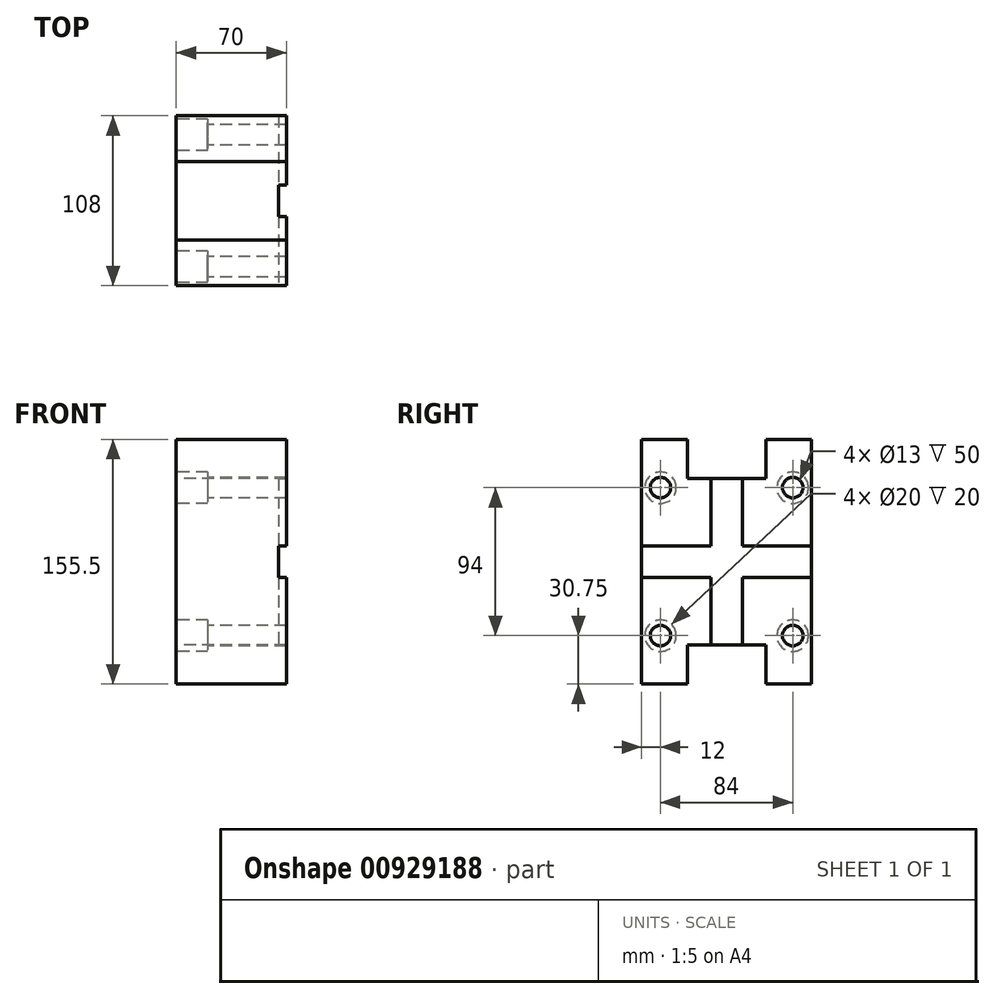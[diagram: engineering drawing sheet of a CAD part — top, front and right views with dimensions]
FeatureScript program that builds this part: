
annotation { "Feature Type Name" : "Feature", "Feature Type Description" : "" }
export const myFeature = defineFeature(function(context is Context, id is Id, definition is map)
    precondition{}
    {
        {
            var Q0;
            Q0=qCreatedBy(makeId("Right.planeOp"),FACE);
            var sketch = newSketch(context, id + "F0", { "sketchPlane" : qUnion([Q0])});
            skLineSegment(sketch, "E0.bottom", {"start": v(54, 77.75) * mm, "end": v(-54, 77.75) * mm});
            skLineSegment(sketch, "E0.top", {"start": v(54, -77.75) * mm, "end": v(-54, -77.75) * mm});
            skLineSegment(sketch, "E0.left", {"start": v(54, 77.75) * mm, "end": v(54, -77.75) * mm});
            skLineSegment(sketch, "E0.right", {"start": v(-54, 77.75) * mm, "end": v(-54, -77.75) * mm});
            skPoint(sketch, "E0.middle", {"position": v(0, 0) * mm});
            skSolve(sketch);
        }
        {
            var Q0;
            Q0 = qSketchRegion(id + "F0", true);
            extrude(context, id + "F1", {"entities" : qUnion([Q0]), "oppositeDirection" : true, "depth" : 70 * mm, "offsetDistance" : 25 * mm});
        }
        {
            var Q0;
            Q0=makeQuery(id+"F1.opExtrude","CAP_FACE",FACE,{"disambiguationData":[OSD([sQuery(id+"F0.wireOp",EDGE,"E0.bottom"),sQuery(id+"F0.wireOp",EDGE,"E0.top"),sQuery(id+"F0.wireOp",EDGE,"E0.left"),sQuery(id+"F0.wireOp",EDGE,"E0.right")])],"isStart":false});
            var sketch = newSketch(context, id + "F2", { "sketchPlane" : qUnion([Q0])});
            skCircle(sketch, "E1", {"center": v(-42, 47) * mm, "radius": 6.5 * mm});
            skCircle(sketch, "E2.MirrorC", {"center": v(42, 47) * mm, "radius": 6.5 * mm});
            skCircle(sketch, "E3.MirrorC", {"center": v(-42, -47) * mm, "radius": 6.5 * mm});
            skCircle(sketch, "E4.MirrorC", {"center": v(42, -47) * mm, "radius": 6.5 * mm});
            skSolve(sketch);
        }
        {
            var Q0;
            Q0 = qSketchRegion(id + "F2", true);
            extrude(context, id + "F3", {"entities" : qUnion([Q0]), "operationType" : NewBodyOperationType.REMOVE, "endBound" : BoundingType.THROUGH_ALL, "oppositeDirection" : true, "depth" : 25 * mm, "offsetDistance" : 25 * mm});
        }
        {
            var Q0;
            Q0=makeQuery(id+"F1.opExtrude","CAP_FACE",FACE,{"disambiguationData":[OSD([sQuery(id+"F0.wireOp",EDGE,"E0.bottom"),sQuery(id+"F0.wireOp",EDGE,"E0.top"),sQuery(id+"F0.wireOp",EDGE,"E0.left"),sQuery(id+"F0.wireOp",EDGE,"E0.right")])],"isStart":false});
            var sketch = newSketch(context, id + "F4", { "sketchPlane" : qUnion([Q0])});
            skLineSegment(sketch, "E5.bottom", {"start": v(25, 77.75) * mm, "end": v(-25, 77.75) * mm});
            skLineSegment(sketch, "E5.top", {"start": v(25, 52.75) * mm, "end": v(-25, 52.75) * mm});
            skLineSegment(sketch, "E5.left", {"start": v(25, 77.75) * mm, "end": v(25, 52.75) * mm});
            skLineSegment(sketch, "E5.right", {"start": v(-25, 77.75) * mm, "end": v(-25, 52.75) * mm});
            skPoint(sketch, "E5.middle", {"position": v(0, 65.25) * mm});
            skLineSegment(sketch, "E6.MirrorCS", {"start": v(25, -52.75) * mm, "end": v(-25, -52.75) * mm});
            skLineSegment(sketch, "E7.MirrorCS", {"start": v(-25, -77.75) * mm, "end": v(-25, -52.75) * mm});
            skLineSegment(sketch, "E8.MirrorCS", {"start": v(25, -77.75) * mm, "end": v(-25, -77.75) * mm});
            skLineSegment(sketch, "E9.MirrorCS", {"start": v(25, -77.75) * mm, "end": v(25, -52.75) * mm});
            skSolve(sketch);
        }
        {
            var Q0;
            Q0 = qSketchRegion(id + "F4", true);
            extrude(context, id + "F5", {"entities" : qUnion([Q0]), "operationType" : NewBodyOperationType.REMOVE, "endBound" : BoundingType.THROUGH_ALL, "oppositeDirection" : true, "depth" : 25 * mm, "offsetDistance" : 25 * mm});
        }
        {
            var Q0;
            Q0=makeQuery(id+"F1.opExtrude","CAP_FACE",FACE,{"disambiguationData":[OSD([sQuery(id+"F0.wireOp",EDGE,"E0.bottom"),sQuery(id+"F0.wireOp",EDGE,"E0.top"),sQuery(id+"F0.wireOp",EDGE,"E0.left"),sQuery(id+"F0.wireOp",EDGE,"E0.right")])],"isStart":false});
            var sketch = newSketch(context, id + "F6", { "sketchPlane" : qUnion([Q0])});
            skCircle(sketch, "E10", {"center": v(-42, 47) * mm, "radius": 10 * mm});
            skCircle(sketch, "E11.0.1.0", {"center": v(-42, -47) * mm, "radius": 10 * mm});
            skCircle(sketch, "E11.1.0.0", {"center": v(42, 47) * mm, "radius": 10 * mm});
            skCircle(sketch, "E11.1.1.0", {"center": v(42, -47) * mm, "radius": 10 * mm});
            skLineSegment(sketch, "E11.direction1", {"start": v(-42, 47) * mm, "end": v(42, 47) * mm, "construction": true});
            skLineSegment(sketch, "E11.direction2", {"start": v(-42, 47) * mm, "end": v(-42, -47) * mm, "construction": true});
            skSolve(sketch);
        }
        {
            var Q0;
            Q0 = qSketchRegion(id + "F6", true);
            extrude(context, id + "F7", {"entities" : qUnion([Q0]), "operationType" : NewBodyOperationType.REMOVE, "oppositeDirection" : true, "depth" : 20 * mm, "offsetDistance" : 25 * mm});
        }
        {
            var Q0;
            Q0=makeQuery(id+"F1.opExtrude","CAP_FACE",FACE,{"disambiguationData":[OSD([sQuery(id+"F0.wireOp",EDGE,"E0.bottom"),sQuery(id+"F0.wireOp",EDGE,"E0.top"),sQuery(id+"F0.wireOp",EDGE,"E0.left"),sQuery(id+"F0.wireOp",EDGE,"E0.right")])],"isStart":true});
            var sketch = newSketch(context, id + "F8", { "sketchPlane" : qUnion([Q0])});
            skLineSegment(sketch, "E12.bottom", {"start": v(-10, 52.75) * mm, "end": v(10, 52.75) * mm});
            skLineSegment(sketch, "E12.top", {"start": v(-10, -52.75) * mm, "end": v(10, -52.75) * mm});
            skLineSegment(sketch, "E12.left", {"start": v(-10, 52.75) * mm, "end": v(-10, -52.75) * mm});
            skLineSegment(sketch, "E12.right", {"start": v(10, 52.75) * mm, "end": v(10, -52.75) * mm});
            skPoint(sketch, "E12.middle", {"position": v(0, 0) * mm});
            skLineSegment(sketch, "E13.bottom", {"start": v(54, 10) * mm, "end": v(-54, 10) * mm});
            skLineSegment(sketch, "E13.top", {"start": v(54, -10) * mm, "end": v(-54, -10) * mm});
            skLineSegment(sketch, "E13.left", {"start": v(54, 10) * mm, "end": v(54, -10) * mm});
            skLineSegment(sketch, "E13.right", {"start": v(-54, 10) * mm, "end": v(-54, -10) * mm});
            skSolve(sketch);
        }
        {
            var Q0;
            Q0 = qSketchRegion(id + "F8", true);
            extrude(context, id + "F9", {"entities" : qUnion([Q0]), "operationType" : NewBodyOperationType.REMOVE, "oppositeDirection" : true, "depth" : 5 * mm, "offsetDistance" : 25 * mm});
        }
    });
